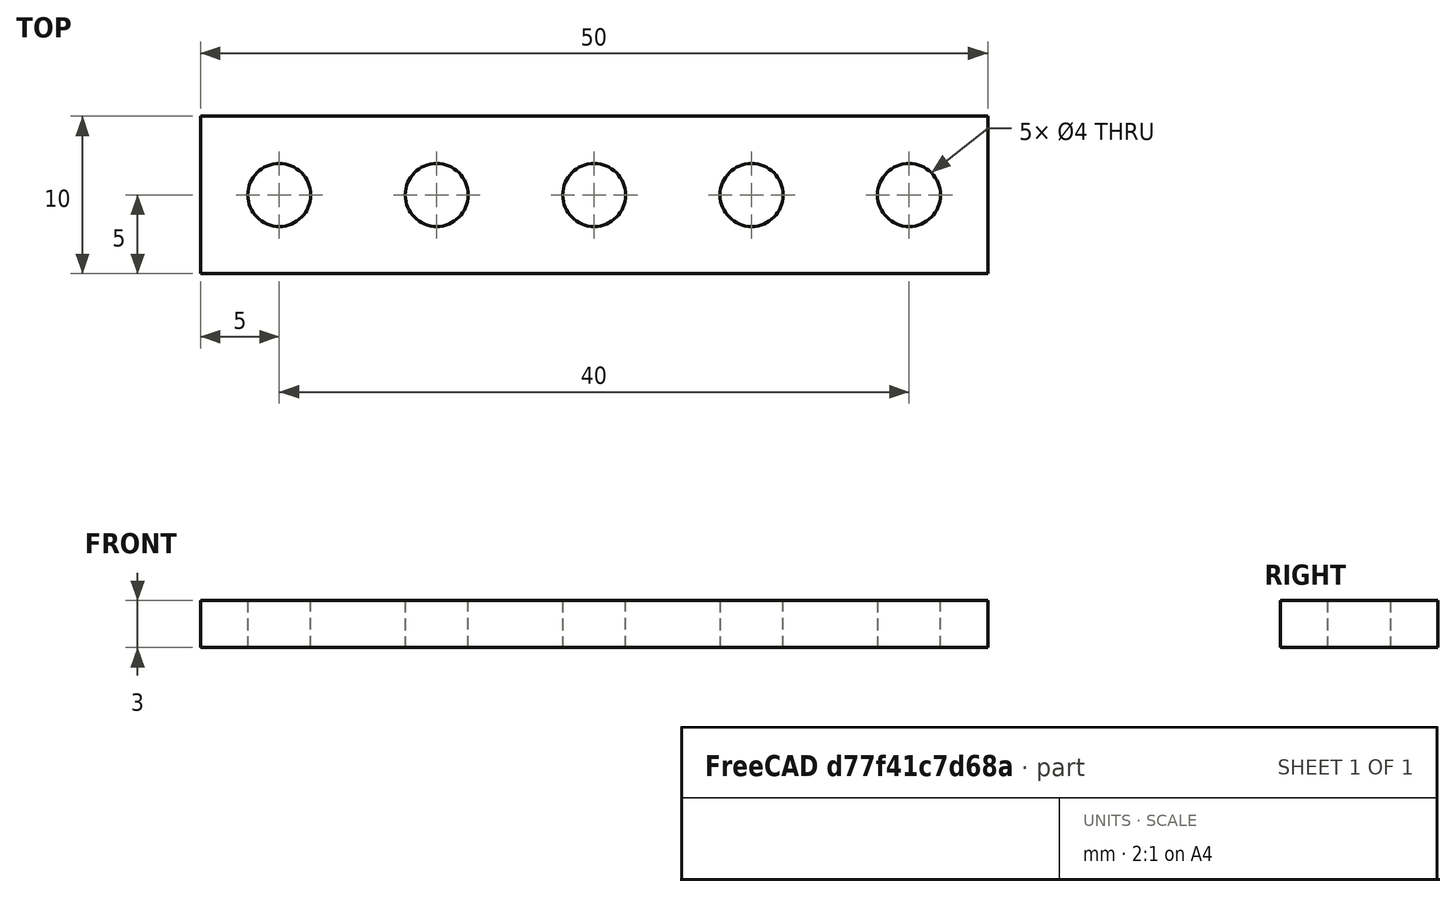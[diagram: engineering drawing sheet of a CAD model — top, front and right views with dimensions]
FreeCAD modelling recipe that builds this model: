
FCSTD DOCUMENT  (FreeCAD 0.19R)
Label: Reto 3
License: All rights reserved
LicenseURL: http://en.wikipedia.org/wiki/All_rights_reserved
objects: Part::Cylinder×5, Part::Cut×5, App::MeasureDistance×5, Part::Box×1
note: 11 computed .brp shape members not serialized (recipe doc carries the construction recipe); baked Part::Feature solids carry a one-line shape summary decoded from their .brp

FEATURE [Part::Box] Box  label="Cubo"
  AttacherType = Attacher::AttachEngine3D
  Height = 3
  Length = 50
  Width = 10
FEATURE [Part::Cylinder] Cylinder  label="Taladro 1"
  Angle = 360
  AttacherType = Attacher::AttachEngine3D
  Height = 10
  Placement = pos=(5,5,-3) rot=(0,0,1;0rad)
  Radius = 2
FEATURE [Part::Cylinder] Cylinder001  label="Taladro 2"
  Angle = 360
  AttacherType = Attacher::AttachEngine3D
  Height = 10
  Placement = pos=(15,5,-3) rot=(0,0,1;0rad)
  Radius = 2
FEATURE [Part::Cylinder] Cylinder002  label="Taladro 3"
  Angle = 360
  AttacherType = Attacher::AttachEngine3D
  Height = 10
  Placement = pos=(25,5,-3) rot=(0,0,1;0rad)
  Radius = 2
FEATURE [Part::Cylinder] Cylinder003  label="Taladro 4"
  Angle = 360
  AttacherType = Attacher::AttachEngine3D
  Height = 10
  Placement = pos=(35,5,-3) rot=(0,0,1;0rad)
  Radius = 2
FEATURE [Part::Cylinder] Cylinder004  label="Taladro 5"
  Angle = 360
  AttacherType = Attacher::AttachEngine3D
  Height = 10
  Placement = pos=(45,5,-3) rot=(0,0,1;0rad)
  Radius = 2
FEATURE [Part::Cut] Cut
  Base = -> Box
  Refine = true
  Tool = -> Cylinder
FEATURE [Part::Cut] Cut001
  Base = -> Cut
  Refine = true
  Tool = -> Cylinder001
FEATURE [Part::Cut] Cut002
  Base = -> Cut001
  Refine = true
  Tool = -> Cylinder002
FEATURE [Part::Cut] Cut003
  Base = -> Cut002
  Refine = true
  Tool = -> Cylinder003
FEATURE [App::MeasureDistance] Distance  label="Distance: 10,15 mm"
  Distance = 10.1493
  P1 = (4.99985,6.98542,3)
  P2 = (15.1491,6.98542,3)
FEATURE [App::MeasureDistance] Distance001  label="Distance: 10,00 mm"
  Distance = 10
  P1 = (0,10,3)
  P2 = (0,0,3)
FEATURE [App::MeasureDistance] Distance002  label="Distance: 3,98 mm"
  Distance = 3.97993
  P1 = (24.7589,6.98542,3)
  P2 = (25.0278,3.01458,3)
FEATURE [Part::Cut] Cut004  label="Reto 3"
  Base = -> Cut003
  Refine = true
  Tool = -> Cylinder004
FEATURE [App::MeasureDistance] Distance003  label="Distance: 3,00 mm"
  Distance = 3
  P1 = (0,0,3)
  P2 = (0,0,0)
FEATURE [App::MeasureDistance] Distance004  label="Distance: 50,00 mm"
  Distance = 50
  P1 = (0,0,3)
  P2 = (50,0,3)
